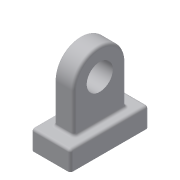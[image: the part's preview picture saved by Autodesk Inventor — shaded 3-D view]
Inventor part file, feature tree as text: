
AUTODESK INVENTOR PART (.ipt)
format: ipt  version: 2014 (Build 180170000, 170)  size: 141,312 bytes
history: native  units: mm
features: extrude x2, fillet x2, sketch x2
ambient origin geometry x8: Origin, YZ Plane, XZ Plane, XY Plane, X Axis, Y Axis, Z Axis, Center Point
bodies: Solid1 (feature_tree)
feature tree (6):
  extrude  "Extrusion1"  Depth=60.0mm
  extrude  "Extrusion3"  Depth=30.0mm
  fillet  "Fillet1"  Radius=20.0mm
  fillet  "Fillet2"  Radius=10.0mm
  sketch  "Sketch1"  dims[d0=30.0mm d1=60.0mm]
  sketch  "Sketch3"  dims[d2=15.0mm d3=0.0mm d10=30.0mm d11=20.0mm d12=10.0mm d13=20.0mm d14=15.0mm d15=0.0mm d16=2.0mm d17=2.0mm]
